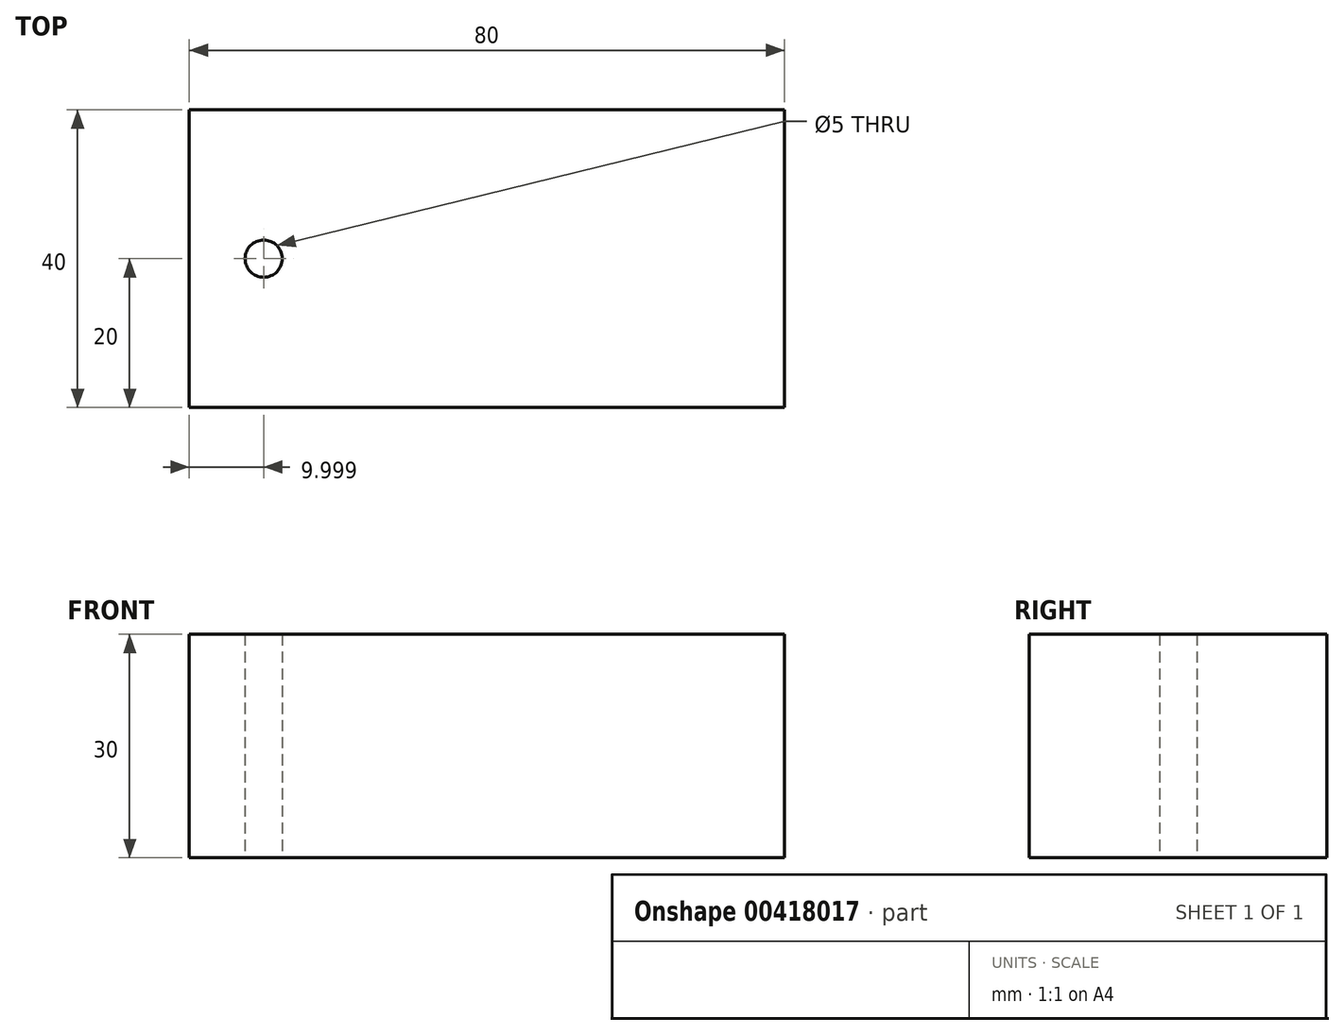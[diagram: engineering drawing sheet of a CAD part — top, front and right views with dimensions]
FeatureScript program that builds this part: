
annotation { "Feature Type Name" : "Feature", "Feature Type Description" : "" }
export const myFeature = defineFeature(function(context is Context, id is Id, definition is map)
    precondition{}
    {
        {
            var Q0;
            Q0=qCreatedBy(makeId("Top.planeOp"),FACE);
            var sketch = newSketch(context, id + "F0", { "sketchPlane" : qUnion([Q0])});
            skLineSegment(sketch, "E0.bottom", {"start": v(-90.05, 61.93) * mm, "end": v(-10.05, 61.93) * mm});
            skLineSegment(sketch, "E0.top", {"start": v(-90.05, 21.93) * mm, "end": v(-10.05, 21.93) * mm});
            skLineSegment(sketch, "E0.left", {"start": v(-90.05, 61.93) * mm, "end": v(-90.05, 21.93) * mm});
            skLineSegment(sketch, "E0.right", {"start": v(-10.05, 61.93) * mm, "end": v(-10.05, 21.93) * mm});
            skCircle(sketch, "E1", {"center": v(-80.05, 41.93) * mm, "radius": 2.5 * mm});
            skPoint(sketch, "E1.centerSnap0", {"position": v(-90.05, 41.93) * mm});
            skSolve(sketch);
        }
        {
            var Q0;
            Q0 = qSketchRegion(id + "F0", true);
            extrude(context, id + "F1", {"entities" : qUnion([Q0]), "depth" : 30 * mm});
        }
    });
